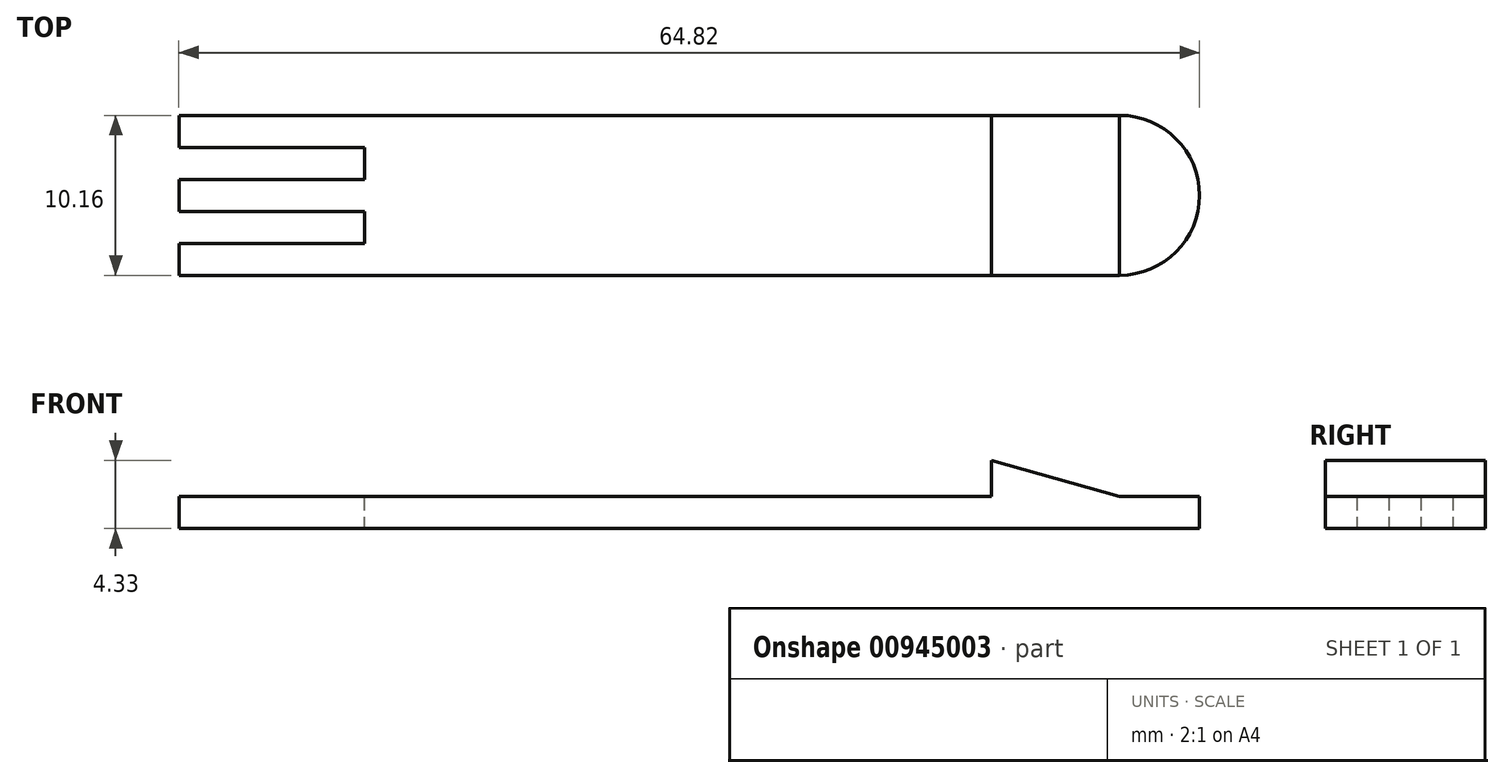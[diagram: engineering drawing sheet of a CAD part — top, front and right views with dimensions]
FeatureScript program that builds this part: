
annotation { "Feature Type Name" : "Feature", "Feature Type Description" : "" }
export const myFeature = defineFeature(function(context is Context, id is Id, definition is map)
    precondition{}
    {
        {
            var Q0;
            Q0=qCreatedBy(makeId("Top.planeOp"),FACE);
            var sketch = newSketch(context, id + "F0", { "sketchPlane" : qUnion([Q0])});
            skLineSegment(sketch, "E0.bottom", {"start": v(-19.76, -30.4) * mm, "end": v(39.98, -30.4) * mm});
            skLineSegment(sketch, "E0.top", {"start": v(-19.76, -40.55) * mm, "end": v(39.98, -40.55) * mm});
            skLineSegment(sketch, "E0.left", {"start": v(-19.76, -30.4) * mm, "end": v(-19.76, -40.55) * mm});
            skLineSegment(sketch, "E0.right", {"start": v(39.98, -30.4) * mm, "end": v(39.98, -40.55) * mm});
            skArc(sketch, "E1", {"start": v(39.98, -40.55) * mm, "mid": v(45.06, -35.47) * mm, "end": v(39.98, -30.4) * mm});
            skSolve(sketch);
        }
        {
            var Q0;
            Q0=qSketchRegion(id+"F0",true);
            extrude(context, id + "F1", {"entities" : qUnion([Q0]), "depth" : 2.03 * mm, "offsetDistance" : 25.4 * mm});
        }
        {
            var Q0;
            Q0=makeQuery(id+"F1.opExtrude","CAP_FACE",FACE,{"disambiguationData":[OSD([sQuery(id+"F0.wireOp",EDGE,"E0.bottom"),sQuery(id+"F0.wireOp",EDGE,"E0.top"),sQuery(id+"F0.wireOp",EDGE,"E0.left"),sQuery(id+"F0.wireOp",EDGE,"E1")])],"isStart":false});
            var sketch = newSketch(context, id + "F2", { "sketchPlane" : qUnion([Q0])});
            skLineSegment(sketch, "E2", {"start": v(-19.76, -32.42) * mm, "end": v(-7.97, -32.42) * mm});
            skLineSegment(sketch, "E3", {"start": v(-19.76, -32.42) * mm, "end": v(-19.76, -30.4) * mm});
            skLineSegment(sketch, "E4", {"start": v(-19.76, -30.4) * mm, "end": v(-19.76, -32.42) * mm});
            skLineSegment(sketch, "E5", {"start": v(-19.76, -34.45) * mm, "end": v(-7.97, -34.45) * mm});
            skLineSegment(sketch, "E6", {"start": v(-19.76, -34.45) * mm, "end": v(-19.76, -32.42) * mm});
            skLineSegment(sketch, "E7", {"start": v(-19.76, -36.49) * mm, "end": v(-7.97, -36.49) * mm});
            skLineSegment(sketch, "E8", {"start": v(-19.76, -36.49) * mm, "end": v(-19.76, -34.45) * mm});
            skLineSegment(sketch, "E9", {"start": v(-19.76, -38.52) * mm, "end": v(-7.97, -38.52) * mm});
            skLineSegment(sketch, "E10", {"start": v(-19.76, -38.52) * mm, "end": v(-19.76, -40.55) * mm});
            skLineSegment(sketch, "E11", {"start": v(-19.76, -40.55) * mm, "end": v(-19.76, -38.52) * mm});
            skLineSegment(sketch, "E12", {"start": v(-7.97, -32.42) * mm, "end": v(-7.97, -34.45) * mm});
            skLineSegment(sketch, "E13", {"start": v(-7.97, -36.49) * mm, "end": v(-7.97, -38.52) * mm});
            skSolve(sketch);
        }
        {
            var Q0;
            Q0=makeQuery(id+"F2.imprint","IMPRINT",FACE,{"disambiguationData":[TD([[makeQuery(id+"F2.imprint","IMPRINT",EDGE,{"derivedFrom":sQuery(id+"F2.wireOp",EDGE,"E2")}),-1.0]])]});
            var Q1;
            {var subQ0=sQuery(id+"F2.wireOp",EDGE,"E7");Q1=makeQuery(id+"F2.imprint","IMPRINT",FACE,{"disambiguationData":[TD([[makeQuery(id+"F2.imprint","IMPRINT",EDGE,{"derivedFrom":subQ0}),-1.0]])]});}
            extrude(context, id + "F3", {"entities" : qUnion([Q0, Q1]), "operationType" : NewBodyOperationType.REMOVE, "oppositeDirection" : true, "depth" : 25.4 * mm, "offsetDistance" : 25.4 * mm});
        }
        {
            var Q0;
            Q0=makeQuery(id+"F1.opExtrude","SWEPT_FACE",FACE,{"disambiguationData":[OSD([sQuery(id+"F0.wireOp",EDGE,"E0.top")])]});
            var sketch = newSketch(context, id + "F4", { "sketchPlane" : qUnion([Q0])});
            skLineSegment(sketch, "E14", {"start": v(39.98, 2.03) * mm, "end": v(31.86, 2.03) * mm});
            skLineSegment(sketch, "E15", {"start": v(31.86, 2.03) * mm, "end": v(31.86, 4.33) * mm});
            skLineSegment(sketch, "E16", {"start": v(31.86, 4.33) * mm, "end": v(39.98, 2.03) * mm});
            skSolve(sketch);
        }
        {
            var Q0;
            Q0 = qSketchRegion(id + "F4", true);
            extrude(context, id + "F5", {"entities" : qUnion([Q0]), "operationType" : NewBodyOperationType.ADD, "oppositeDirection" : true, "depth" : 10.16 * mm, "offsetDistance" : 25.4 * mm});
        }
    });
